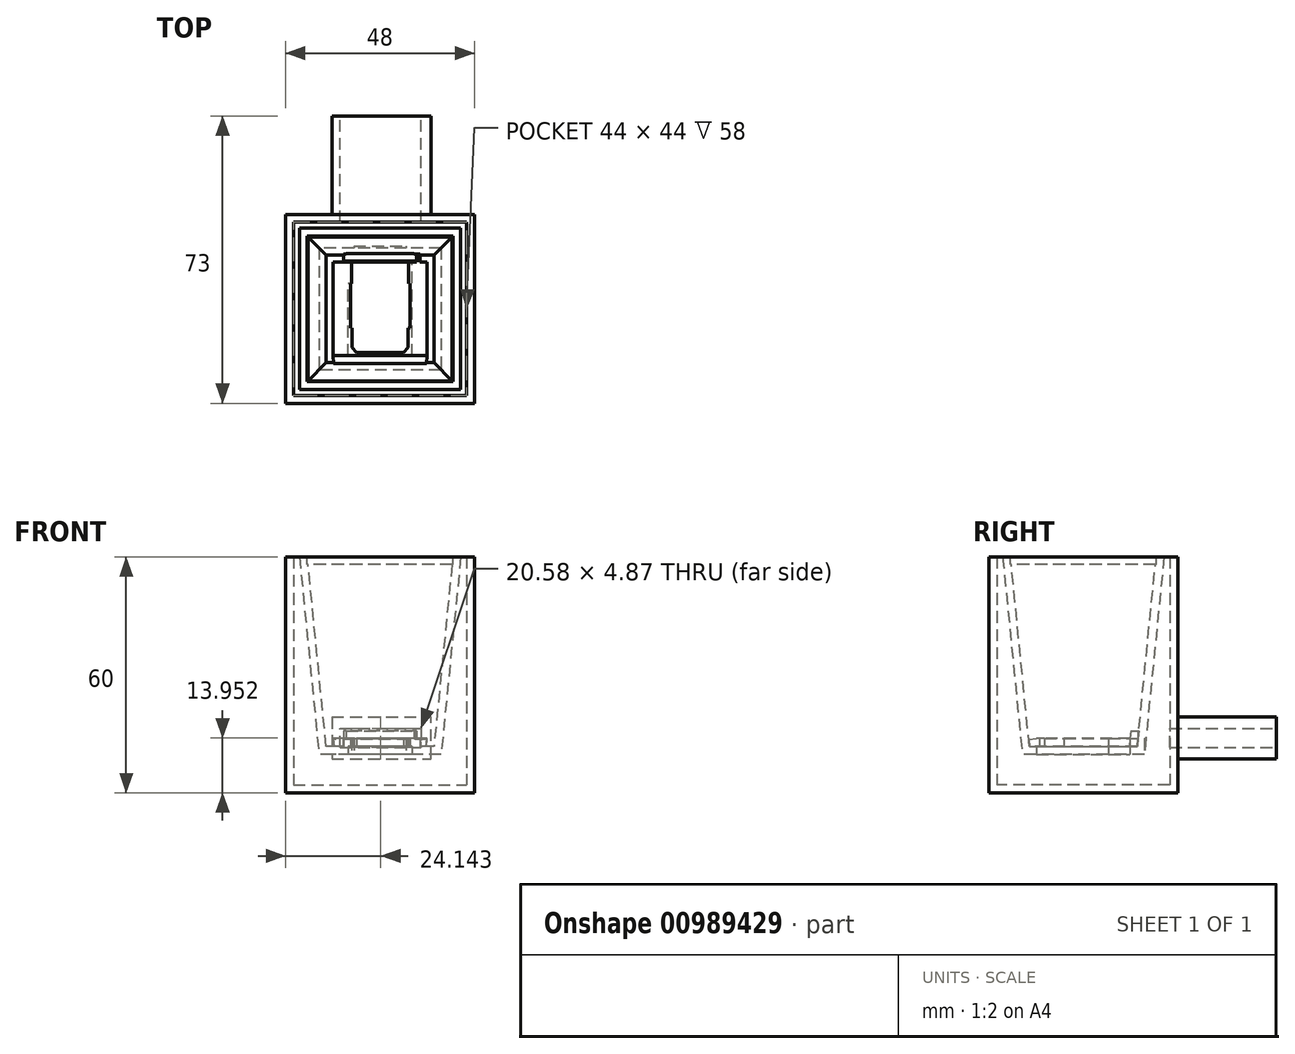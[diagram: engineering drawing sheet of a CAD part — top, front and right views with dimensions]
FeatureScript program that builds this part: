
annotation { "Feature Type Name" : "Feature", "Feature Type Description" : "" }
export const myFeature = defineFeature(function(context is Context, id is Id, definition is map)
    precondition{}
    {
        {
            var Q0;
            Q0=qCreatedBy(makeId("Top.planeOp"),FACE);
            var sketch = newSketch(context, id + "F0", { "sketchPlane" : qUnion([Q0])});
            skLineSegment(sketch, "E0.bottom", {"start": v(15.5, 15.5) * mm, "end": v(-15.5, 15.5) * mm});
            skLineSegment(sketch, "E0.top", {"start": v(15.5, -15.5) * mm, "end": v(-15.5, -15.5) * mm});
            skLineSegment(sketch, "E0.left", {"start": v(15.5, 15.5) * mm, "end": v(15.5, -15.5) * mm});
            skLineSegment(sketch, "E0.right", {"start": v(-15.5, 15.5) * mm, "end": v(-15.5, -15.5) * mm});
            skPoint(sketch, "E0.middle", {"position": v(0, 0) * mm});
            skSolve(sketch);
        }
        {
            var Q0;
            Q0=qCreatedBy(makeId("Top.planeOp"),FACE);
            cPlane(context, id + "F1", {"entities" : qUnion([Q0]), "cplaneType" : CPlaneType.OFFSET, "offset" : 50.2 * mm, "width" : 150 * mm, "height" : 150 * mm});
        }
        {
            var Q0;
            Q0=qCreatedBy(id+"F1.planeOp",FACE);
            var sketch = newSketch(context, id + "F2", { "sketchPlane" : qUnion([Q0])});
            skLineSegment(sketch, "E1.bottom", {"start": v(20.5, 20.5) * mm, "end": v(-20.5, 20.5) * mm});
            skLineSegment(sketch, "E1.top", {"start": v(20.5, -20.5) * mm, "end": v(-20.5, -20.5) * mm});
            skLineSegment(sketch, "E1.left", {"start": v(20.5, 20.5) * mm, "end": v(20.5, -20.5) * mm});
            skLineSegment(sketch, "E1.right", {"start": v(-20.5, 20.5) * mm, "end": v(-20.5, -20.5) * mm});
            skPoint(sketch, "E1.middle", {"position": v(0, 0) * mm});
            skSolve(sketch);
        }
        {
            var Q0;
            Q0=makeQuery(id+"F2.imprint","IMPRINT",FACE,{"disambiguationData":[TD([[makeQuery(id+"F2.imprint","IMPRINT",EDGE,{"derivedFrom":sQuery(id+"F2.wireOp",EDGE,"E1.bottom")}),1.0]])]});
            var Q1;
            Q1=makeQuery(id+"F0.imprint","IMPRINT",FACE,{"disambiguationData":[TD([[makeQuery(id+"F0.imprint","IMPRINT",EDGE,{"derivedFrom":sQuery(id+"F0.wireOp",EDGE,"E0.bottom")}),1.0]])]});
            loft(context, id + "F3", {"sheetProfilesArray" : [{ "sheetProfileEntities" : qUnion([Q0]) }, { "sheetProfileEntities" : qUnion([Q1]) }]});
        }
        {
            var Q0;
            Q0=makeQuery(id+"F3.opLoft","CAP_FACE",FACE,{"disambiguationData":[OSD([makeQuery(id+"F2.imprint","IMPRINT",FACE,{"disambiguationData":[TD([[makeQuery(id+"F2.imprint","IMPRINT",EDGE,{"derivedFrom":sQuery(id+"F2.wireOp",EDGE,"E1.bottom")}),1.0]])]})])],"isStart":true});
            shell(context, id + "F4", {"entities" : qUnion([Q0]), "thickness" : 4 * mm});
        }
        {
            var Q0;
            Q0=makeQuery(id+"F3.opLoft","CAP_FACE",FACE,{"disambiguationData":[OSD([makeQuery(id+"F0.imprint","IMPRINT",FACE,{"disambiguationData":[TD([[makeQuery(id+"F0.imprint","IMPRINT",EDGE,{"derivedFrom":sQuery(id+"F0.wireOp",EDGE,"E0.bottom")}),1.0]])]})])],"isStart":true});
            var sketch = newSketch(context, id + "F5", { "sketchPlane" : qUnion([Q0])});
            skLineSegment(sketch, "E2.bottom", {"start": v(8.16, 11.9) * mm, "end": v(-8.16, 11.9) * mm});
            skLineSegment(sketch, "E2.top", {"start": v(8.16, -11.9) * mm, "end": v(-8.16, -11.9) * mm});
            skLineSegment(sketch, "E2.left", {"start": v(8.16, 11.9) * mm, "end": v(8.16, -11.9) * mm});
            skLineSegment(sketch, "E2.right", {"start": v(-8.16, 11.9) * mm, "end": v(-8.16, -11.9) * mm});
            skPoint(sketch, "E2.middle", {"position": v(0, 0) * mm});
            skPoint(sketch, "E3", {"position": v(6.62, -11.9) * mm});
            skPoint(sketch, "E4", {"position": v(-6.62, -11.9) * mm});
            skLineSegment(sketch, "E5.bottom", {"start": v(8.16, 11.9) * mm, "end": v(7.36, 11.9) * mm});
            skLineSegment(sketch, "E5.top", {"start": v(8.16, 11.1) * mm, "end": v(7.36, 11.1) * mm});
            skLineSegment(sketch, "E5.left", {"start": v(8.16, 11.9) * mm, "end": v(8.16, 11.1) * mm});
            skLineSegment(sketch, "E5.right", {"start": v(7.36, 11.9) * mm, "end": v(7.36, 11.1) * mm});
            skLineSegment(sketch, "E6", {"start": v(7.36, 11.1) * mm, "end": v(-8.16, 11.1) * mm});
            skPoint(sketch, "E7", {"position": v(-7.16, 4.9) * mm});
            skPoint(sketch, "E8.MirrorP", {"position": v(7.16, 4.9) * mm});
            skLineSegment(sketch, "E9.bottom", {"start": v(8.16, 11.9) * mm, "end": v(7.16, 11.9) * mm});
            skLineSegment(sketch, "E9.top", {"start": v(8.16, 4.9) * mm, "end": v(7.16, 4.9) * mm});
            skLineSegment(sketch, "E9.left", {"start": v(8.16, 11.9) * mm, "end": v(8.16, 4.9) * mm});
            skLineSegment(sketch, "E9.right", {"start": v(7.16, 11.9) * mm, "end": v(7.16, 4.9) * mm});
            skLineSegment(sketch, "E10.bottom", {"start": v(-8.16, 11.9) * mm, "end": v(-7.16, 11.9) * mm});
            skLineSegment(sketch, "E10.top", {"start": v(-8.16, 4.9) * mm, "end": v(-7.16, 4.9) * mm});
            skLineSegment(sketch, "E10.left", {"start": v(-8.16, 11.9) * mm, "end": v(-8.16, 4.9) * mm});
            skLineSegment(sketch, "E10.right", {"start": v(-7.16, 11.9) * mm, "end": v(-7.16, 4.9) * mm});
            skPoint(sketch, "E11", {"position": v(-7.26, -6.4) * mm});
            skLineSegment(sketch, "E12.bottom", {"start": v(-7.26, -6.4) * mm, "end": v(-8.16, -6.4) * mm});
            skLineSegment(sketch, "E12.top", {"start": v(-7.26, -11.9) * mm, "end": v(-8.16, -11.9) * mm});
            skLineSegment(sketch, "E12.left", {"start": v(-7.26, -6.4) * mm, "end": v(-7.26, -11.9) * mm});
            skLineSegment(sketch, "E12.right", {"start": v(-8.16, -6.4) * mm, "end": v(-8.16, -11.9) * mm});
            skLineSegment(sketch, "E13.MirrorCS", {"start": v(7.26, -6.4) * mm, "end": v(7.26, -11.9) * mm});
            skLineSegment(sketch, "E14.MirrorCS", {"start": v(7.26, -6.4) * mm, "end": v(8.16, -6.4) * mm});
            skPoint(sketch, "E15", {"position": v(-7.76, 0.75) * mm});
            skLineSegment(sketch, "E16", {"start": v(-7.56, 4.9) * mm, "end": v(-7.56, -6.4) * mm});
            skLineSegment(sketch, "E17.MirrorCS", {"start": v(7.56, 4.9) * mm, "end": v(7.56, -6.4) * mm});
            skLineSegment(sketch, "E18.bottom", {"start": v(6.62, -11.9) * mm, "end": v(-6.62, -11.9) * mm});
            skLineSegment(sketch, "E18.top", {"start": v(6.62, -23.6) * mm, "end": v(-6.62, -23.6) * mm});
            skLineSegment(sketch, "E18.left", {"start": v(6.62, -11.9) * mm, "end": v(6.62, -23.6) * mm});
            skLineSegment(sketch, "E18.right", {"start": v(-6.62, -11.9) * mm, "end": v(-6.62, -23.6) * mm});
            skPoint(sketch, "E19", {"position": v(-8.16, 8.9) * mm});
            skPoint(sketch, "E20", {"position": v(-5.16, 11.9) * mm});
            skLineSegment(sketch, "E21", {"start": v(-8.16, 8.9) * mm, "end": v(-5.16, 11.9) * mm});
            skLineSegment(sketch, "E22", {"start": v(0, 0) * mm, "end": v(0, 11.9) * mm});
            skLineSegment(sketch, "E23.MirrorCS", {"start": v(8.16, 8.9) * mm, "end": v(5.16, 11.9) * mm});
            skSolve(sketch);
        }
        {
            var Q0;
            {var subQ0=sQuery(id+"F5.wireOp",EDGE,"E18.bottom");Q0=makeQuery(id+"F5.imprint","IMPRINT",FACE,{"disambiguationData":[TD([[makeQuery(id+"F5.imprint","IMPRINT",EDGE,{"derivedFrom":subQ0}),1.0]])]});}
            var Q1;
            {var subQ0=sQuery(id+"F5.wireOp",EDGE,"E18.top");Q1=makeQuery(id+"F5.imprint","IMPRINT",FACE,{"disambiguationData":[TD([[makeQuery(id+"F5.imprint","IMPRINT",EDGE,{"derivedFrom":subQ0}),-1.0]])]});}
            var Q2;
            {var subQ1=sQuery(id+"F5.wireOp",EDGE,"E13.MirrorCS");Q2=makeQuery(id+"F5.imprint","IMPRINT",FACE,{"disambiguationData":[TD([[makeQuery(id+"F5.imprint","IMPRINT",EDGE,{"derivedFrom":subQ1}),1.0]])]});}
            var Q3;
            {var subQ0=sQuery(id+"F5.wireOp",EDGE,"E12.left");Q3=makeQuery(id+"F5.imprint","IMPRINT",FACE,{"disambiguationData":[TD([[makeQuery(id+"F5.imprint","IMPRINT",EDGE,{"derivedFrom":subQ0}),1.0]])]});}
            var Q4;
            {var subQ7=sQuery(id+"F5.wireOp",EDGE,"E5.top");Q4=makeQuery(id+"F5.imprint","IMPRINT",FACE,{"disambiguationData":[TD([[makeQuery(id+"F5.imprint","IMPRINT",EDGE,{"derivedFrom":subQ7}),1.0]])]});}
            var Q5;
            {var subQ0=sQuery(id+"F5.wireOp",EDGE,"E5.top");Q5=makeQuery(id+"F5.imprint","IMPRINT",FACE,{"disambiguationData":[TD([[makeQuery(id+"F5.imprint","IMPRINT",EDGE,{"derivedFrom":subQ0}),-1.0]])]});}
            var Q6;
            {var subQ0=sQuery(id+"F5.wireOp",EDGE,"E5.right");Q6=makeQuery(id+"F5.imprint","IMPRINT",FACE,{"disambiguationData":[TD([[makeQuery(id+"F5.imprint","IMPRINT",EDGE,{"derivedFrom":subQ0}),-1.0]])]});}
            var Q7;
            {var subQ0=sQuery(id+"F5.wireOp",EDGE,"E2.bottom");Q7=makeQuery(id+"F5.imprint","IMPRINT",FACE,{"disambiguationData":[TD([[makeQuery(id+"F5.imprint","IMPRINT",EDGE,{"derivedFrom":subQ0}),1.0]])]});}
            var Q8;
            {var subQ5=sQuery(id+"F5.wireOp",EDGE,"E17.MirrorCS");Q8=makeQuery(id+"F5.imprint","IMPRINT",FACE,{"disambiguationData":[TD([[makeQuery(id+"F5.imprint","IMPRINT",EDGE,{"derivedFrom":subQ5}),1.0]])]});}
            var Q9;
            {var subQ0=sQuery(id+"F5.wireOp",EDGE,"E10.left");var subQ3=sQuery(id+"F5.wireOp",EDGE,"E6");var subQ4=makeQuery(id+"F5.imprint","INTERSECT",VERTEX,{"derivedFrom":[subQ3,subQ0]});Q9=makeQuery(id+"F5.imprint","IMPRINT",FACE,{"disambiguationData":[TD([[makeQuery(id+"F5.imprint","IMPRINT",EDGE,{"disambiguationData":[TD([[subQ4,1.0]])],"derivedFrom":subQ3}),1.0]])]});}
            var Q10;
            {var subQ5=sQuery(id+"F5.wireOp",EDGE,"E10.bottom");Q10=makeQuery(id+"F5.imprint","IMPRINT",FACE,{"disambiguationData":[TD([[makeQuery(id+"F5.imprint","IMPRINT",EDGE,{"derivedFrom":subQ5}),-1.0]])]});}
            var Q11;
            {var subQ0=sQuery(id+"F5.wireOp",EDGE,"E2.right");Q11=makeQuery(id+"F5.imprint","IMPRINT",FACE,{"disambiguationData":[TD([[makeQuery(id+"F5.imprint","IMPRINT",EDGE,{"derivedFrom":subQ0}),1.0]])]});}
            var Q12;
            Q12=makeQuery(id+"F5.imprint","IMPRINT",FACE,{"disambiguationData":[TD([[makeQuery(id+"F5.imprint","IMPRINT",EDGE,{"derivedFrom":sQuery(id+"F5.wireOp",EDGE,"E12.top")}),-1.0]])]});
            var Q13;
            {var subQ0=sQuery(id+"F5.wireOp",EDGE,"E21");var subQ1=sQuery(id+"F5.wireOp",EDGE,"E6");var subQ2=makeQuery(id+"F5.imprint","INTERSECT",VERTEX,{"derivedFrom":[subQ1,subQ0]});Q13=makeQuery(id+"F5.imprint","IMPRINT",FACE,{"disambiguationData":[TD([[makeQuery(id+"F5.imprint","IMPRINT",EDGE,{"disambiguationData":[TD([[subQ2,-1.0]])],"derivedFrom":subQ1}),1.0]])]});}
            var Q14;
            {var subQ0=sQuery(id+"F5.wireOp",EDGE,"E10.right");var subQ1=sQuery(id+"F5.wireOp",EDGE,"E10.top");var subQ2=makeQuery(id+"F5.imprint","INTERSECT",VERTEX,{"derivedFrom":[subQ1,subQ0]});Q14=makeQuery(id+"F5.imprint","IMPRINT",FACE,{"disambiguationData":[TD([[makeQuery(id+"F5.imprint","IMPRINT",EDGE,{"disambiguationData":[TD([[subQ2,1.0]])],"derivedFrom":subQ1}),1.0]])]});}
            var Q15;
            {var subQ0=sQuery(id+"F5.wireOp",EDGE,"E9.right");var subQ1=sQuery(id+"F5.wireOp",EDGE,"E9.top");var subQ2=makeQuery(id+"F5.imprint","INTERSECT",VERTEX,{"derivedFrom":[subQ1,subQ0]});Q15=makeQuery(id+"F5.imprint","IMPRINT",FACE,{"disambiguationData":[TD([[makeQuery(id+"F5.imprint","IMPRINT",EDGE,{"disambiguationData":[TD([[subQ2,1.0]])],"derivedFrom":subQ1}),-1.0]])]});}
            var Q16;
            {var subQ0=sQuery(id+"F5.wireOp",EDGE,"E9.right");var subQ1=sQuery(id+"F5.wireOp",EDGE,"E6");var subQ2=makeQuery(id+"F5.imprint","INTERSECT",VERTEX,{"derivedFrom":[subQ1,subQ0]});Q16=makeQuery(id+"F5.imprint","IMPRINT",FACE,{"disambiguationData":[TD([[makeQuery(id+"F5.imprint","IMPRINT",EDGE,{"disambiguationData":[TD([[subQ2,-1.0]])],"derivedFrom":subQ1}),1.0]])]});}
            extrude(context, id + "F6", {"entities" : qUnion([Q0, Q1, Q2, Q3, Q4, Q5, Q6, Q7, Q8, Q9, Q10, Q11, Q12, Q13, Q14, Q15, Q16]), "operationType" : NewBodyOperationType.REMOVE, "oppositeDirection" : true, "depth" : 2 * mm, "offsetDistance" : 25 * mm});
        }
        {
            var Q0;
            {var subQ0=sQuery(id+"F5.wireOp",EDGE,"E12.left");Q0=makeQuery(id+"F5.imprint","IMPRINT",FACE,{"disambiguationData":[TD([[makeQuery(id+"F5.imprint","IMPRINT",EDGE,{"derivedFrom":subQ0}),1.0]])]});}
            var Q1;
            {var subQ0=sQuery(id+"F5.wireOp",EDGE,"E18.bottom");Q1=makeQuery(id+"F5.imprint","IMPRINT",FACE,{"disambiguationData":[TD([[makeQuery(id+"F5.imprint","IMPRINT",EDGE,{"derivedFrom":subQ0}),1.0]])]});}
            var Q2;
            {var subQ0=sQuery(id+"F5.wireOp",EDGE,"E18.top");Q2=makeQuery(id+"F5.imprint","IMPRINT",FACE,{"disambiguationData":[TD([[makeQuery(id+"F5.imprint","IMPRINT",EDGE,{"derivedFrom":subQ0}),-1.0]])]});}
            extrude(context, id + "F7", {"entities" : qUnion([Q0, Q1, Q2]), "operationType" : NewBodyOperationType.REMOVE, "oppositeDirection" : true, "depth" : 4 * mm, "offsetDistance" : 25 * mm});
        }
        {
            var Q0;
            Q0=makeQuery(id+"F4.opShell","OFFSET_FACE",FACE,{"disambiguationData":[OSD([sQuery(id+"F0.wireOp",EDGE,"E0.bottom"),sQuery(id+"F0.wireOp",EDGE,"E0.top"),sQuery(id+"F0.wireOp",EDGE,"E0.right"),sQuery(id+"F2.wireOp",EDGE,"E1.bottom"),sQuery(id+"F2.wireOp",EDGE,"E1.top"),sQuery(id+"F2.wireOp",EDGE,"E1.right")])]});
            var Q1;
            Q1=makeQuery(id+"F4.opShell","OFFSET_FACE",FACE,{"disambiguationData":[OSD([sQuery(id+"F0.wireOp",EDGE,"E0.bottom"),sQuery(id+"F0.wireOp",EDGE,"E0.top"),sQuery(id+"F0.wireOp",EDGE,"E0.left"),sQuery(id+"F2.wireOp",EDGE,"E1.bottom"),sQuery(id+"F2.wireOp",EDGE,"E1.top"),sQuery(id+"F2.wireOp",EDGE,"E1.left")])]});
            var Q2;
            Q2=makeQuery(id+"F4.opShell","OFFSET_FACE",FACE,{"disambiguationData":[OSD([sQuery(id+"F0.wireOp",EDGE,"E0.bottom"),sQuery(id+"F0.wireOp",EDGE,"E0.left"),sQuery(id+"F0.wireOp",EDGE,"E0.right"),sQuery(id+"F2.wireOp",EDGE,"E1.bottom"),sQuery(id+"F2.wireOp",EDGE,"E1.left"),sQuery(id+"F2.wireOp",EDGE,"E1.right")])]});
            shell(context, id + "F8", {"entities" : qUnion([Q0, Q1, Q2]), "thickness" : 2 * mm});
        }
        {
            var Q0;
            Q0=makeQuery(id+"F3.opLoft","CAP_FACE",FACE,{"disambiguationData":[OSD([makeQuery(id+"F2.imprint","IMPRINT",FACE,{"disambiguationData":[TD([[makeQuery(id+"F2.imprint","IMPRINT",EDGE,{"derivedFrom":sQuery(id+"F2.wireOp",EDGE,"E1.bottom")}),1.0]])]})])],"isStart":true});
            var sketch = newSketch(context, id + "F9", { "sketchPlane" : qUnion([Q0])});
            skPoint(sketch, "E24", {"position": v(18.5, 18.5) * mm});
            skPoint(sketch, "E25", {"position": v(-18.5, -18.5) * mm});
            skLineSegment(sketch, "E26.bottom", {"start": v(18.5, 18.5) * mm, "end": v(-18.5, 18.5) * mm});
            skLineSegment(sketch, "E26.top", {"start": v(18.5, -18.5) * mm, "end": v(-18.5, -18.5) * mm});
            skLineSegment(sketch, "E26.left", {"start": v(18.5, 18.5) * mm, "end": v(18.5, -18.5) * mm});
            skLineSegment(sketch, "E26.right", {"start": v(-18.5, 18.5) * mm, "end": v(-18.5, -18.5) * mm});
            skLineSegment(sketch, "E27.bottom", {"start": v(3.94, 4.92) * mm, "end": v(-4.02, 4.92) * mm});
            skLineSegment(sketch, "E27.top", {"start": v(3.94, -7.7) * mm, "end": v(-4.02, -7.7) * mm});
            skLineSegment(sketch, "E27.left", {"start": v(3.94, 4.92) * mm, "end": v(3.94, -7.7) * mm});
            skLineSegment(sketch, "E27.right", {"start": v(-4.02, 4.92) * mm, "end": v(-4.02, -7.7) * mm});
            skSolve(sketch);
        }
        {
            var Q0;
            Q0=makeQuery(id+"F4.opShell","OFFSET_FACE",FACE,{"disambiguationData":[OSD([sQuery(id+"F0.wireOp",EDGE,"E0.top"),sQuery(id+"F0.wireOp",EDGE,"E0.left"),sQuery(id+"F0.wireOp",EDGE,"E0.right"),sQuery(id+"F2.wireOp",EDGE,"E1.top"),sQuery(id+"F2.wireOp",EDGE,"E1.left"),sQuery(id+"F2.wireOp",EDGE,"E1.right")])]});
            extrude(context, id + "F10", {"entities" : qUnion([Q0]), "operationType" : NewBodyOperationType.REMOVE, "oppositeDirection" : true, "depth" : 2 * mm, "offsetDistance" : 25 * mm});
        }
        {
            var Q0;
            Q0=makeQuery(id+"F9.imprint","IMPRINT",FACE,{"disambiguationData":[TD([[makeQuery(id+"F9.imprint","IMPRINT",EDGE,{"derivedFrom":sQuery(id+"F9.wireOp",EDGE,"E27.bottom")}),-1.0]])]});
            var Q1;
            Q1=makeQuery(id+"F9.imprint","IMPRINT",FACE,{"disambiguationData":[TD([[makeQuery(id+"F9.imprint","IMPRINT",EDGE,{"derivedFrom":sQuery(id+"F9.wireOp",EDGE,"E26.bottom")}),1.0]])]});
            extrude(context, id + "F11", {"entities" : qUnion([Q0, Q1]), "operationType" : NewBodyOperationType.REMOVE, "oppositeDirection" : true, "depth" : 2 * mm, "offsetDistance" : 25 * mm});
        }
        {
            var Q0;
            Q0=qCreatedBy(id+"F1.planeOp",FACE);
            cPlane(context, id + "F12", {"entities" : qUnion([Q0]), "cplaneType" : CPlaneType.OFFSET, "offset" : 60 * mm, "oppositeDirection" : true, "width" : 150 * mm, "height" : 150 * mm});
        }
        {
            var Q0;
            Q0=qCreatedBy(id+"F12.planeOp",FACE);
            var sketch = newSketch(context, id + "F13", { "sketchPlane" : qUnion([Q0])});
            skLineSegment(sketch, "E28.bottom", {"start": v(-24, 24) * mm, "end": v(24, 24) * mm});
            skLineSegment(sketch, "E28.top", {"start": v(-24, -24) * mm, "end": v(24, -24) * mm});
            skLineSegment(sketch, "E28.left", {"start": v(-24, 24) * mm, "end": v(-24, -24) * mm});
            skLineSegment(sketch, "E28.right", {"start": v(24, 24) * mm, "end": v(24, -24) * mm});
            skPoint(sketch, "E28.middle", {"position": v(0, 0) * mm});
            skSolve(sketch);
        }
        {
            var Q0;
            Q0 = qSketchRegion(id + "F13", true);
            var Q1;
            Q1=qCreatedBy(id+"F1.planeOp",FACE);
            extrude(context, id + "F14", {"entities" : qUnion([Q0]), "endBound" : BoundingType.UP_TO_SURFACE, "depth" : 60 * mm, "endBoundEntityFace" : qUnion([Q1]), "offsetDistance" : 25 * mm});
        }
        {
            var Q0;
            Q0=makeQuery(id+"F14.opExtrude","CAP_FACE",FACE,{"disambiguationData":[OSD([sQuery(id+"F13.wireOp",EDGE,"E28.bottom"),sQuery(id+"F13.wireOp",EDGE,"E28.top"),sQuery(id+"F13.wireOp",EDGE,"E28.left"),sQuery(id+"F13.wireOp",EDGE,"E28.right")])],"isStart":false});
            shell(context, id + "F15", {"entities" : qUnion([Q0]), "thickness" : 2 * mm});
        }
        {
            var Q0;
            Q0=makeQuery(id+"F14.opExtrude","SWEPT_FACE",FACE,{"disambiguationData":[OSD([sQuery(id+"F13.wireOp",EDGE,"E28.bottom")])]});
            var sketch = newSketch(context, id + "F16", { "sketchPlane" : qUnion([Q0])});
            skLineSegment(sketch, "E29", {"start": v(10.15, 6.59) * mm, "end": v(-10.43, 6.59) * mm});
            skLineSegment(sketch, "E30", {"start": v(10.15, 3.2) * mm, "end": v(10.15, 6.59) * mm});
            skLineSegment(sketch, "E31", {"start": v(-10.43, 6.59) * mm, "end": v(-10.43, 3.2) * mm});
            skLineSegment(sketch, "E32.bottom", {"start": v(12.22, -1.2) * mm, "end": v(-12.95, -1.2) * mm});
            skLineSegment(sketch, "E32.top", {"start": v(12.22, 9.5) * mm, "end": v(-12.95, 9.5) * mm});
            skLineSegment(sketch, "E32.left", {"start": v(12.22, 0.78) * mm, "end": v(12.22, 9.5) * mm});
            skLineSegment(sketch, "E32.right", {"start": v(-12.95, 0.78) * mm, "end": v(-12.95, 9.5) * mm});
            skLineSegment(sketch, "E33", {"start": v(10.15, 6.59) * mm, "end": v(10.15, 1.72) * mm});
            skLineSegment(sketch, "E34", {"start": v(10.15, 1.72) * mm, "end": v(-10.43, 1.72) * mm});
            skLineSegment(sketch, "E35", {"start": v(-10.43, 1.72) * mm, "end": v(-10.43, 6.59) * mm});
            skLineSegment(sketch, "E36", {"start": v(12.22, 0.78) * mm, "end": v(12.22, -1.2) * mm});
            skLineSegment(sketch, "E37", {"start": v(-12.95, 0.78) * mm, "end": v(-12.95, -1.2) * mm});
            skSolve(sketch);
        }
        {
            var Q0;
            Q0=makeQuery(id+"F16.imprint","IMPRINT",FACE,{"disambiguationData":[TD([[makeQuery(id+"F16.imprint","IMPRINT",EDGE,{"derivedFrom":sQuery(id+"F16.wireOp",EDGE,"E29")}),1.0]])]});
            extrude(context, id + "F17", {"entities" : qUnion([Q0]), "operationType" : NewBodyOperationType.REMOVE, "oppositeDirection" : true, "depth" : 2 * mm, "offsetDistance" : 25 * mm});
        }
        {
            var Q0;
            Q0 = qSketchRegion(id + "F16", true);
            extrude(context, id + "F18", {"entities" : qUnion([Q0]), "operationType" : NewBodyOperationType.ADD, "depth" : 25 * mm, "offsetDistance" : 25 * mm});
        }
    });
